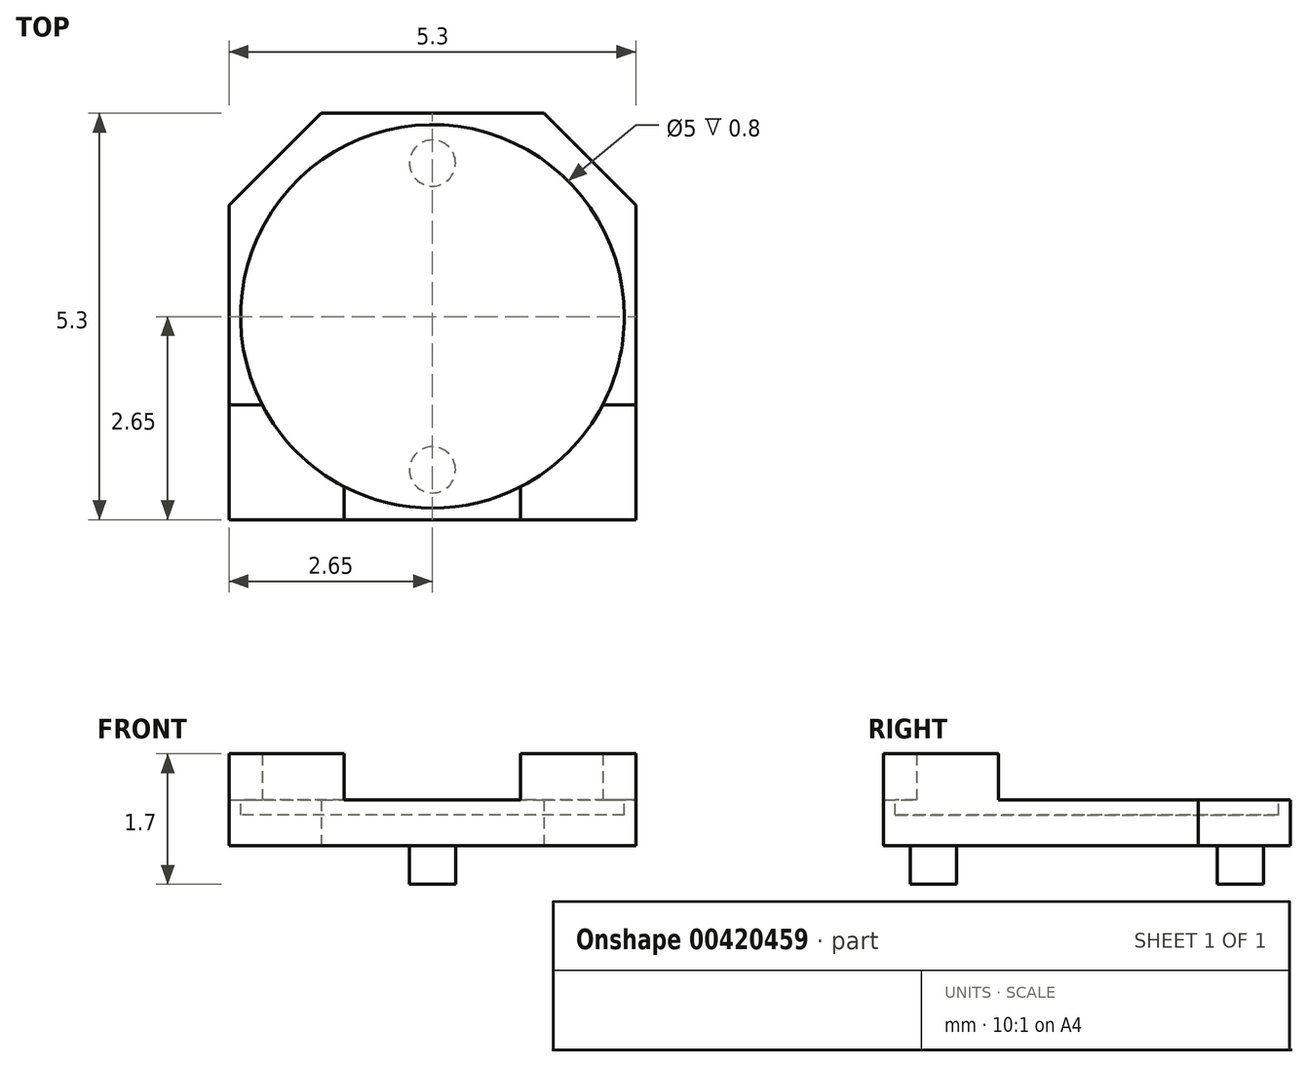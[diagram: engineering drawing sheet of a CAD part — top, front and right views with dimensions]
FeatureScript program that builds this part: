
annotation { "Feature Type Name" : "Feature", "Feature Type Description" : "" }
export const myFeature = defineFeature(function(context is Context, id is Id, definition is map)
    precondition{}
    {
        {
            var Q0;
            Q0=qCreatedBy(makeId("Top.planeOp"),FACE);
            var sketch = newSketch(context, id + "F0", { "sketchPlane" : qUnion([Q0]), "disableImprinting" : false});
            skCircle(sketch, "E0", {"center": v(0, 0) * mm, "radius": 2.5 * mm, "construction": true});
            skLineSegment(sketch, "E1.bottom", {"start": v(-2.65, -2.65) * mm, "end": v(2.65, -2.65) * mm});
            skLineSegment(sketch, "E1.top", {"start": v(-1.45, 2.65) * mm, "end": v(1.45, 2.65) * mm});
            skLineSegment(sketch, "E1.left", {"start": v(-2.65, -2.65) * mm, "end": v(-2.65, 1.45) * mm});
            skLineSegment(sketch, "E1.right", {"start": v(2.65, -2.65) * mm, "end": v(2.65, 1.45) * mm});
            skLineSegment(sketch, "E2", {"start": v(-2.65, 1.45) * mm, "end": v(-1.45, 2.65) * mm});
            skLineSegment(sketch, "E3", {"start": v(1.45, 2.65) * mm, "end": v(2.65, 1.45) * mm});
            skSolve(sketch);
        }
        {
            var Q0;
            Q0 = qSketchRegion(id + "F0", true);
            extrude(context, id + "F1", {"entities" : qUnion([Q0]), "depth" : 0.6 * mm});
        }
        {
            var Q0;
            Q0=makeQuery(id+"F1.opExtrude","CAP_FACE",FACE,{"disambiguationData":[OSD([sQuery(id+"F0.wireOp",EDGE,"E1.bottom"),sQuery(id+"F0.wireOp",EDGE,"E1.top"),sQuery(id+"F0.wireOp",EDGE,"E1.left"),sQuery(id+"F0.wireOp",EDGE,"E1.right"),sQuery(id+"F0.wireOp",EDGE,"E2"),sQuery(id+"F0.wireOp",EDGE,"E3")])],"isStart":false});
            var sketch = newSketch(context, id + "F2", { "sketchPlane" : qUnion([Q0])});
            skCircle(sketch, "E4", {"center": v(0, 0) * mm, "radius": 2.5 * mm});
            skSolve(sketch);
        }
        {
            var Q0;
            Q0 = qSketchRegion(id + "F2", true);
            extrude(context, id + "F3", {"entities" : qUnion([Q0]), "operationType" : NewBodyOperationType.REMOVE, "oppositeDirection" : true, "depth" : 0.2 * mm});
        }
        {
            var Q0;
            Q0=makeQuery(id+"F1.opExtrude","CAP_FACE",FACE,{"disambiguationData":[OSD([sQuery(id+"F0.wireOp",EDGE,"E1.bottom"),sQuery(id+"F0.wireOp",EDGE,"E1.top"),sQuery(id+"F0.wireOp",EDGE,"E1.left"),sQuery(id+"F0.wireOp",EDGE,"E1.right"),sQuery(id+"F0.wireOp",EDGE,"E2"),sQuery(id+"F0.wireOp",EDGE,"E3")])],"isStart":false});
            var sketch = newSketch(context, id + "F4", { "sketchPlane" : qUnion([Q0])});
            skLineSegment(sketch, "E5", {"start": v(-2.65, -1.15) * mm, "end": v(-2.65, -2.65) * mm});
            skLineSegment(sketch, "E6", {"start": v(-2.65, -2.65) * mm, "end": v(-1.15, -2.65) * mm});
            skLineSegment(sketch, "E7", {"start": v(-1.15, -2.65) * mm, "end": v(-1.15, -2.22) * mm});
            skLineSegment(sketch, "E8", {"start": v(-2.65, -1.15) * mm, "end": v(-2.22, -1.15) * mm});
            skArc(sketch, "E9", {"start": v(-2.22, -1.15) * mm, "mid": v(-1.77, -1.77) * mm, "end": v(-1.15, -2.22) * mm});
            skLineSegment(sketch, "E10", {"start": v(2.65, -1.15) * mm, "end": v(2.22, -1.15) * mm});
            skLineSegment(sketch, "E11", {"start": v(2.65, -1.15) * mm, "end": v(2.65, -2.65) * mm});
            skLineSegment(sketch, "E12", {"start": v(2.65, -2.65) * mm, "end": v(1.15, -2.65) * mm});
            skLineSegment(sketch, "E13", {"start": v(1.15, -2.65) * mm, "end": v(1.15, -2.22) * mm});
            skArc(sketch, "E14", {"start": v(1.15, -2.22) * mm, "mid": v(1.77, -1.77) * mm, "end": v(2.22, -1.15) * mm});
            skSolve(sketch);
        }
        {
            var Q0;
            Q0 = qSketchRegion(id + "F4", true);
            extrude(context, id + "F5", {"entities" : qUnion([Q0]), "operationType" : NewBodyOperationType.ADD, "depth" : 0.6 * mm});
        }
        {
            var Q0;
            Q0=makeQuery(id+"F1.opExtrude","CAP_FACE",FACE,{"disambiguationData":[OSD([sQuery(id+"F0.wireOp",EDGE,"E1.bottom"),sQuery(id+"F0.wireOp",EDGE,"E1.top"),sQuery(id+"F0.wireOp",EDGE,"E1.left"),sQuery(id+"F0.wireOp",EDGE,"E1.right"),sQuery(id+"F0.wireOp",EDGE,"E2"),sQuery(id+"F0.wireOp",EDGE,"E3")])],"isStart":true});
            var sketch = newSketch(context, id + "F6", { "sketchPlane" : qUnion([Q0])});
            skCircle(sketch, "E15", {"center": v(0, 2) * mm, "radius": 0.3 * mm});
            skCircle(sketch, "E16", {"center": v(0, -2) * mm, "radius": 0.3 * mm});
            skSolve(sketch);
        }
        {
            var Q0;
            Q0 = qSketchRegion(id + "F6", true);
            extrude(context, id + "F7", {"entities" : qUnion([Q0]), "operationType" : NewBodyOperationType.ADD, "depth" : 0.5 * mm});
        }
    });
